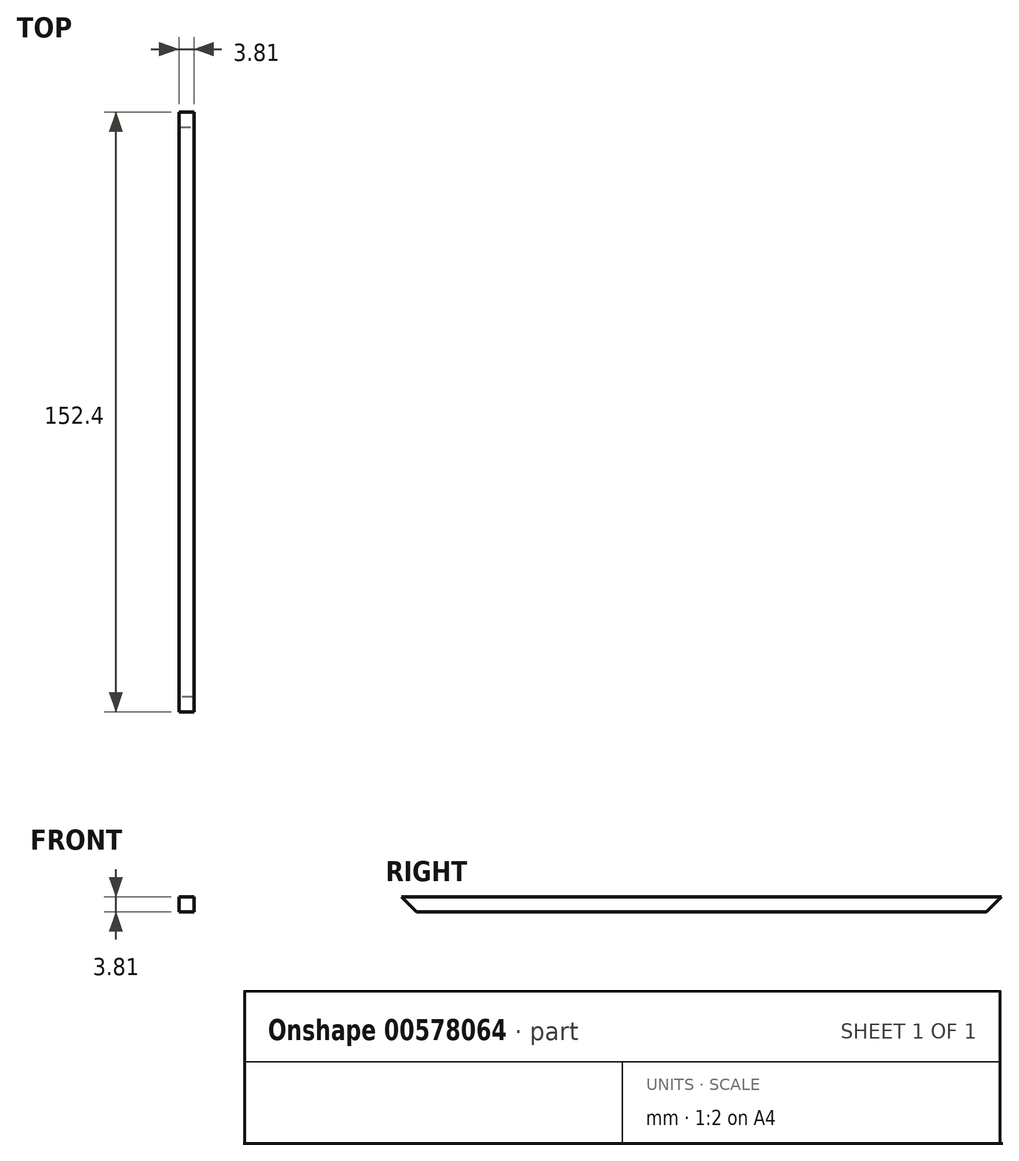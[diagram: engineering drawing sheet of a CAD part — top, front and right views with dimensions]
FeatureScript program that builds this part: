
annotation { "Feature Type Name" : "Feature", "Feature Type Description" : "" }
export const myFeature = defineFeature(function(context is Context, id is Id, definition is map)
    precondition{}
    {
        {
            var Q0;
            Q0=qCreatedBy(makeId("Top.planeOp"),FACE);
            var sketch = newSketch(context, id + "F0", { "sketchPlane" : qUnion([Q0])});
            skLineSegment(sketch, "E0.bottom", {"start": v(-50.8, 100.97) * mm, "end": v(-46.98, 100.97) * mm});
            skLineSegment(sketch, "E0.top", {"start": v(-50.8, -51.43) * mm, "end": v(-46.98, -51.43) * mm});
            skLineSegment(sketch, "E0.left", {"start": v(-50.8, 100.97) * mm, "end": v(-50.8, -51.43) * mm});
            skLineSegment(sketch, "E0.right", {"start": v(-46.98, 100.97) * mm, "end": v(-46.98, -51.43) * mm});
            skSolve(sketch);
        }
        {
            var Q0;
            Q0=makeQuery(id+"F0.imprint","IMPRINT",FACE,{"disambiguationData":[TD([[makeQuery(id+"F0.imprint","IMPRINT",EDGE,{"derivedFrom":sQuery(id+"F0.wireOp",EDGE,"E0.bottom")}),-1.0]])]});
            extrude(context, id + "F1", {"entities" : qUnion([Q0]), "depth" : 3.8 * mm, "offsetDistance" : 25.4 * mm});
        }
        {
            var Q0;
            Q0=makeQuery(id+"F1.opExtrude","CAP_EDGE",EDGE,{"disambiguationData":[OSD([sQuery(id+"F0.wireOp",EDGE,"E0.top")])],"isStart":true});
            chamfer(context, id + "F2", {"entities" : qUnion([Q0]), "width" : 3.8 * mm, "tangentPropagation" : true});
        }
        {
            var Q0;
            Q0=makeQuery(id+"F1.opExtrude","CAP_EDGE",EDGE,{"disambiguationData":[OSD([sQuery(id+"F0.wireOp",EDGE,"E0.bottom")])],"isStart":true});
            chamfer(context, id + "F3", {"entities" : qUnion([Q0]), "width" : 3.8 * mm, "tangentPropagation" : true});
        }
    });
